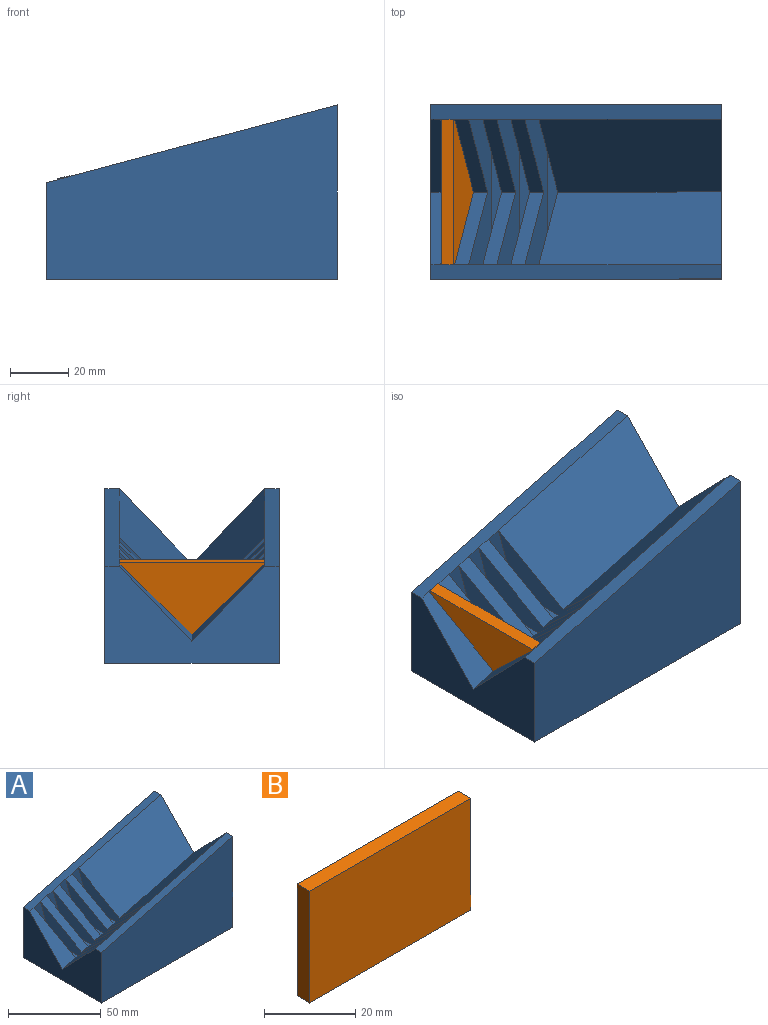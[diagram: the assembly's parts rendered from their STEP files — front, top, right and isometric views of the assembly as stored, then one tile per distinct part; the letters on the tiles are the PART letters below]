
ASSEMBLY  parts=2 mates=1
PART A: 37 faces, bbox 100x60x60 mm
  f0: plane 62.79x40.97mm, normal (-0.18,0.71,0.68), area 2179.7mm2, adj f1,f6,f23,f25
  f1: plane 62.79x40.97mm, normal (-0.18,-0.71,0.68), area 2179.7mm2, adj f0,f6,f25,f29
  f2: plane 30.27x12.59mm, normal (0,-1,0), area 150mm2, adj f4,f5,f6,f29
  f3: plane 30.27x12.59mm, normal (0,1,0), area 150mm2, adj f4,f5,f6,f23
  f4: plane 50x4.83mm, normal (-0.26,0,0.97), area 250mm2, adj f2,f3,f5,f6
  f5: plane 50x28.98mm, normal (0.97,0,0.26), area 875mm2, adj f2,f3,f4,f7,f8
  f6: plane 50x28.98mm, normal (-0.97,0,-0.26), area 875mm2, adj f0,f1,f2,f3,f4
  f7: plane 25.44x25mm, normal (-0.18,0.71,0.68), area 176.8mm2, adj f5,f8,f13,f23
  f8: plane 25.44x25mm, normal (-0.18,-0.71,0.68), area 176.8mm2, adj f5,f7,f13,f29
  f9: plane 30.27x12.59mm, normal (0,-1,0), area 150mm2, adj f11,f12,f13,f29
  f10: plane 30.27x12.59mm, normal (0,1,0), area 150mm2, adj f11,f12,f13,f23
  f11: plane 50x4.83mm, normal (-0.26,0,0.97), area 250mm2, adj f9,f10,f12,f13
  f12: plane 50x28.98mm, normal (0.97,0,0.26), area 875mm2, adj f9,f10,f11,f14,f15
  f13: plane 50x28.98mm, normal (-0.97,0,-0.26), area 875mm2, adj f7,f8,f9,f10,f11
  f14: plane 25.44x25mm, normal (-0.18,0.71,0.68), area 176.8mm2, adj f12,f15,f20,f23
  f15: plane 25.44x25mm, normal (-0.18,-0.71,0.68), area 176.8mm2, adj f12,f14,f20,f29
  f16: plane 30.27x12.59mm, normal (0,-1,0), area 150mm2, adj f18,f19,f20,f29
  f17: plane 30.27x12.59mm, normal (0,1,0), area 150mm2, adj f18,f19,f20,f23
  f18: plane 50x4.83mm, normal (-0.26,0,0.97), area 250mm2, adj f16,f17,f19,f20
  f19: plane 50x28.98mm, normal (0.97,0,0.26), area 875mm2, adj f16,f17,f18,f30,f31
  f20: plane 50x28.98mm, normal (-0.97,0,-0.26), area 875mm2, adj f14,f15,f16,f17,f18
  f21: plane 26.8x25mm, normal (-0.18,0.71,0.68), area 243.1mm2, adj f22,f23,f24,f36
  f22: plane 26.8x25mm, normal (-0.18,-0.71,0.68), area 243.1mm2, adj f21,f24,f29,f36
  f23: plane 100x26.8mm, normal (-0.26,0,0.97), area 517.6mm2, adj f0,f3,f7,f10,f14,f17,f21,f24
  f24: plane 60x33.21mm, normal (-1,0,0), area 1345.3mm2, adj f21,f22,f23,f26,f27,f28,f29
  f25: plane 60x60mm, normal (1,0,0), area 2953mm2, adj f0,f1,f23,f26,f27,f28,f29
  f26: plane 100x60mm, normal (0,1,0), area 4660.3mm2, adj f24,f25,f28,f29
  f27: plane 100x60mm, normal (0,-1,0), area 4660.3mm2, adj f23,f24,f25,f28
  f28: plane 100x60mm, normal (0,0,-1), area 6000mm2, adj f24,f25,f26,f27
  f29: plane 100x26.8mm, normal (-0.26,0,0.97), area 517.6mm2, adj f1,f2,f8,f9,f15,f16,f22,f24
  f30: plane 25.44x25mm, normal (-0.18,0.71,0.68), area 176.8mm2, adj f19,f23,f31,f35
  f31: plane 25.44x25mm, normal (-0.18,-0.71,0.68), area 176.8mm2, adj f19,f29,f30,f35
  f32: plane 30.27x12.59mm, normal (0,-1,0), area 150mm2, adj f29,f34,f35,f36
  f33: plane 30.27x12.59mm, normal (0,1,0), area 150mm2, adj f23,f34,f35,f36
  f34: plane 50x4.83mm, normal (-0.26,0,0.97), area 250mm2, adj f32,f33,f35,f36
  f35: plane 50x28.98mm, normal (-0.97,0,-0.26), area 875mm2, adj f30,f31,f32,f33,f34
  f36: plane 50x28.98mm, normal (0.97,0,0.26), area 875mm2, adj f21,f22,f32,f33,f34
PART B: 6 faces, bbox 50x4x30 mm
  f0: plane 50x4mm, normal (0,0,-1), area 200mm2, adj f1,f3,f4,f5
  f1: plane 30x4mm, normal (1,0,0), area 120mm2, adj f0,f2,f4,f5
  f2: plane 50x4mm, normal (0,0,1), area 200mm2, adj f1,f3,f4,f5
  f3: plane 30x4mm, normal (-1,0,0), area 120mm2, adj f0,f2,f4,f5
  f4: plane 50x30mm, normal (0,-1,0), area 1500mm2, adj f0,f1,f2,f3
  f5: plane 50x30mm, normal (0,1,0), area 1500mm2, adj f0,f1,f2,f3
PLACE A at identity fixed
PLACE B rot(axis=(0.13,-0.13,-0.98),91deg) t=(-38.44,0,21.08)mm
MATE slider A.f34 <-> B.f0  axis (-0.26,0,0.97) through (-36.41,0,5.79)mm
